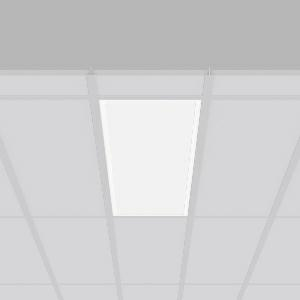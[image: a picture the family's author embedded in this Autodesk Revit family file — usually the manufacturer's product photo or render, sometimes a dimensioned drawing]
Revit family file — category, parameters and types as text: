
# Revit family: sidelite_eco_672372_002_1ef7
name_source: partatom
category: Lighting Fixtures
units: mm (PartAtom-declared; Revit-internal decimal feet)

## family parameters
Cut with Voids When Loaded = No
Host = Face
Light Source = No
Part Type = Normal
Room Calculation Point = No
Round Connector Dimension = Use Diameter
Shared = No

## types (1)
- SIDELITE ECO (1 x LED Modul 830, 3300 lm, 3000)
    Apparent Load = 29 VA
    CIE Flux Codes = 46 79 96 100 100
    Color Rendering = 80
    Color Temperature = 3000
    Default Elevation = 1800 mm
    Description = Series: SIDELITE ECO
Highly economical recessed luminaire with progressive LED technology. For escape route illumination. Frame made of aluminium, powder-coated. Diffuser: plastic, opal. Lightguide and diffuser made of non-yellowing plastic (PMMA). Lateral light emission (RZB SIDELITE technology) for homogeneous light distribution. External driver. Self-contained system with automatic self-test. External driver with simple plug-in locking system. Extended connection cable (1.90 m). 
Colour: white
Length: 1195 mm
Width: 295 mm
Cut-out length: 1170 mm
Cut-out width: 270 mm
Recess height: 160 mm
Luminaire: recess height: 40 mm
Weight: 4.4 kg
Operating mode: maintained power mode
Duration time: 8 h
Lamp: LED
Socket: without socket
Colour temperature: 3000K
Colour rendering index (CRI): 80
System power: 29 W
Rated luminous flux: 3300 lm
Luminous flux, emergency: 220 lm
System power, emergency: -
Control gear: Regulated power supply
Protection class: I
Type of protection: IP 40
    Height = 0 mm  [stored 0 ft]
    Lamp = 1 x LED Modul 830
    Lamp Light Flux = 3300 lm
    Lamp count = 1
    Length = 1195 mm
    Lifetime = 50000 h
    Luminous efficacy = 114 lm/W
    Manufacturer = RZB
    ModVariant = No
    Model = 672372.002
    Mounting Place = Ceiling
    Mounting Type = Recessed
    Number of Poles = 1
    OnlyDefault = Yes
    Power Factor = 1
    Product Name = SIDELITE ECO
    Product group = Recessed modular luminaires
    ProductGroupID = 406
    Protection Class = Protection class I
    Protection Degree = IP 40
    RLX_Detail_Level = 1
    RLX_Emergency_Light_Flux = 220 lm
    RLX_Emergency_Type = 3
    RLX_Emergency_Type_DB = Yes
    RlxData = <blob elided: 30697 chars, md5=ebc1dae6>
    Socket = socket
    Standby Power = 0 W
    System Light Flux = 3300 lm
    System Power = 29 W
    Type Comments = Product without accessories
    Type Image = 312365.002.jpg
    URL = http://relux.com
    VarID = ---
    Voltage = 230 V
    Voltage Range = 220-240 V
    Weight = 0.00 kg
    Width = 295 mm

note: [stored X ft] marks values corroborated as IEEE doubles in the binary element streams (Revit-internal decimal feet)

## geometry (parser evidence)
native form markers: Blend x4, Sweep x9
no freeform markers — native parametric forms only
